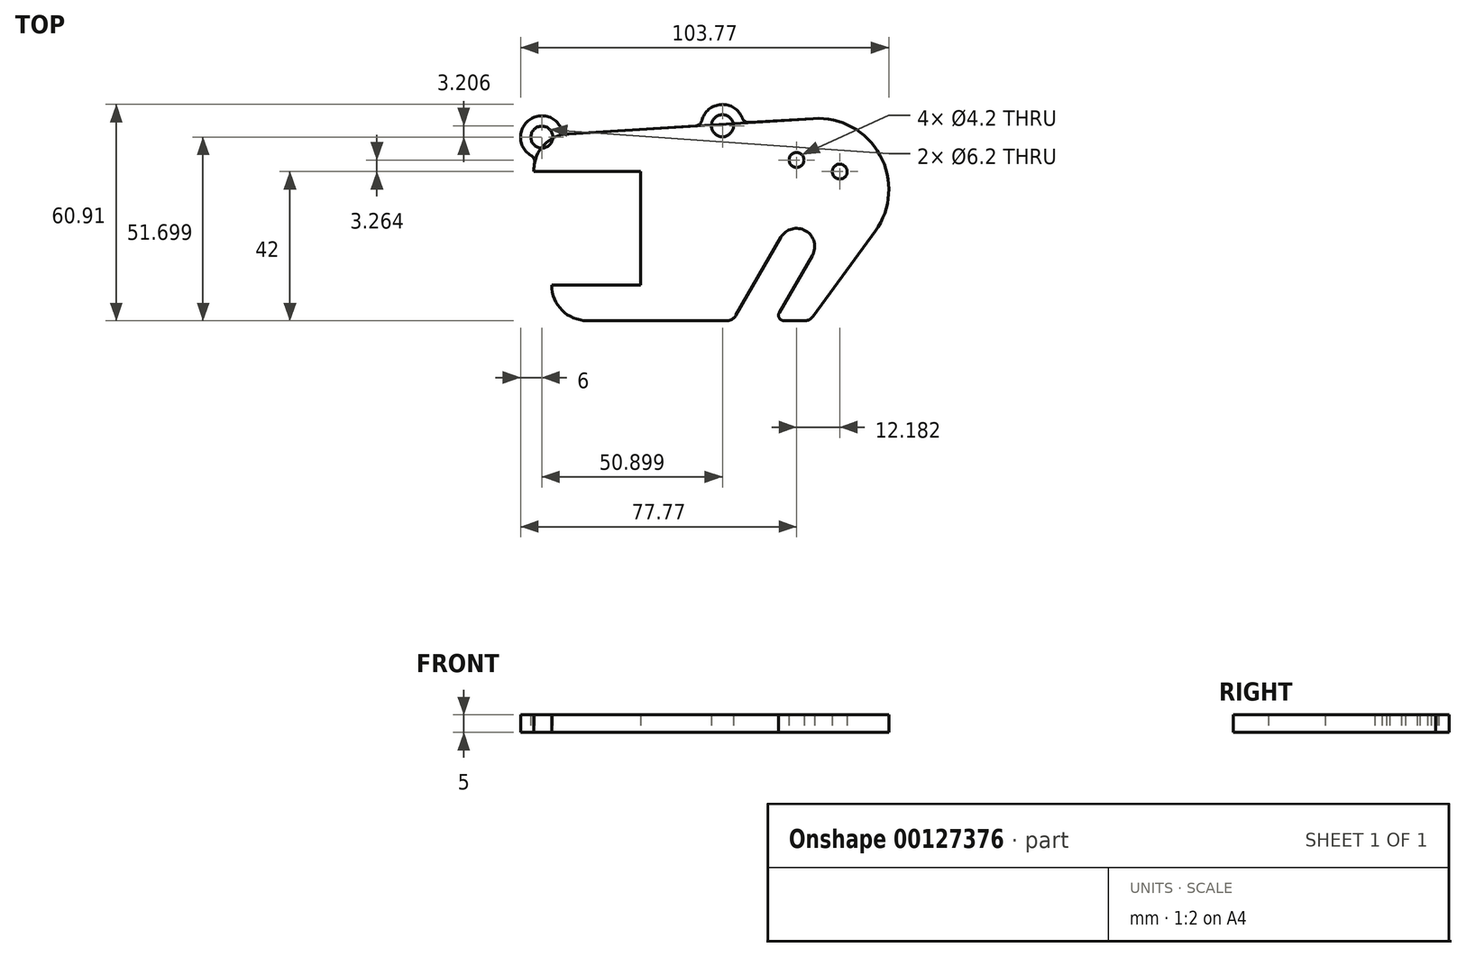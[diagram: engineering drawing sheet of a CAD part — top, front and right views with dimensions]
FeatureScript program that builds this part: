
annotation { "Feature Type Name" : "Feature", "Feature Type Description" : "" }
export const myFeature = defineFeature(function(context is Context, id is Id, definition is map)
    precondition{}
    {
        {
            var Q0;
            Q0=qCreatedBy(makeId("Top.planeOp"),FACE);
            var sketch = newSketch(context, id + "F0", { "sketchPlane" : qUnion([Q0])});
            skLineSegment(sketch, "E0", {"start": v(-25, 17) * mm, "end": v(-25, -15) * mm});
            skLineSegment(sketch, "E1", {"start": v(-25, 1) * mm, "end": v(19, 1) * mm, "construction": true});
            skLineSegment(sketch, "E2", {"start": v(19, 1) * mm, "end": v(19, -4.1) * mm, "construction": true});
            skLineSegment(sketch, "E3", {"start": v(-25, 17) * mm, "end": v(25, 17) * mm, "construction": true});
            skArc(sketch, "E4", {"start": v(23.42, -6.65) * mm, "mid": v(21.55, 0.32) * mm, "end": v(14.58, -1.55) * mm});
            skLineSegment(sketch, "E5", {"start": v(-25, 17) * mm, "end": v(-55, 17) * mm});
            skLineSegment(sketch, "E6", {"start": v(-25, -15) * mm, "end": v(-50, -15) * mm});
            skLineSegment(sketch, "E7", {"start": v(-50, -15) * mm, "end": v(-50, -15) * mm});
            skLineSegment(sketch, "E8", {"start": v(-40, -25) * mm, "end": v(-0.69, -25) * mm});
            skLineSegment(sketch, "E9", {"start": v(-55, 17) * mm, "end": v(-55, 17.61) * mm});
            skLineSegment(sketch, "E10", {"start": v(14.58, -1.55) * mm, "end": v(1.91, -23.5) * mm});
            skLineSegment(sketch, "E11", {"start": v(-45.63, 27.6) * mm, "end": v(23.74, 31.96) * mm});
            skPoint(sketch, "E12.visualSharp", {"position": v(67.74, 34.73) * mm});
            skArc(sketch, "E12.filletArc", {"start": v(41.18, 0.24) * mm, "mid": v(42.53, 21.63) * mm, "end": v(23.74, 31.96) * mm});
            skLineSegment(sketch, "E13", {"start": v(25, 12) * mm, "end": v(25, 17) * mm, "construction": true});
            skLineSegment(sketch, "E14", {"start": v(15.42, -25) * mm, "end": v(21.3, -25) * mm});
            skLineSegment(sketch, "E15", {"start": v(23.42, -6.65) * mm, "end": v(14.12, -22.75) * mm});
            skLineSegment(sketch, "E16", {"start": v(41.18, 0.24) * mm, "end": v(23.72, -23.76) * mm});
            skLineSegment(sketch, "E17", {"start": v(25, 17) * mm, "end": v(31.18, 17) * mm, "construction": true});
            skLineSegment(sketch, "E18", {"start": v(19, -4.1) * mm, "end": v(31.18, 17) * mm, "construction": true});
            skLineSegment(sketch, "E19", {"start": v(19, 1) * mm, "end": v(19, 20.26) * mm, "construction": true});
            skArc(sketch, "E20", {"start": v(31.18, 17) * mm, "mid": v(25.3, 19.43) * mm, "end": v(19, 20.26) * mm, "construction": true});
            skCircle(sketch, "E21", {"center": v(31.18, 17) * mm, "radius": 2.1 * mm});
            skCircle(sketch, "E22", {"center": v(19, 20.26) * mm, "radius": 2.1 * mm});
            skPoint(sketch, "E23.visualSharp", {"position": v(-55, 27) * mm});
            skArc(sketch, "E23.filletArc", {"start": v(-45.63, 27.6) * mm, "mid": v(-52.29, 24.46) * mm, "end": v(-55, 17.61) * mm});
            skPoint(sketch, "E24.visualSharp", {"position": v(-50, -25) * mm});
            skArc(sketch, "E24.filletArc", {"start": v(-50, -15) * mm, "mid": v(-47.07, -22.07) * mm, "end": v(-40, -25) * mm});
            skPoint(sketch, "E25.visualSharp", {"position": v(1.04, -25) * mm});
            skArc(sketch, "E25.filletArc", {"start": v(-0.69, -25) * mm, "mid": v(0.81, -24.6) * mm, "end": v(1.91, -23.5) * mm});
            skPoint(sketch, "E26.visualSharp", {"position": v(12.82, -25) * mm});
            skArc(sketch, "E26.filletArc", {"start": v(14.12, -22.75) * mm, "mid": v(14.12, -24.25) * mm, "end": v(15.42, -25) * mm});
            skPoint(sketch, "E27.visualSharp", {"position": v(22.82, -25) * mm});
            skArc(sketch, "E27.filletArc", {"start": v(21.3, -25) * mm, "mid": v(22.66, -24.67) * mm, "end": v(23.72, -23.76) * mm});
            skLineSegment(sketch, "E28", {"start": v(-25, -15) * mm, "end": v(0, -15) * mm, "construction": true});
            skLineSegment(sketch, "E29", {"start": v(0, -15) * mm, "end": v(0, 0) * mm, "construction": true});
            skSolve(sketch);
        }
        {
            var Q0;
            Q0=makeQuery(id+"F0.imprint","IMPRINT",FACE,{"disambiguationData":[TD([[makeQuery(id+"F0.imprint","IMPRINT",EDGE,{"derivedFrom":sQuery(id+"F0.wireOp",EDGE,"E0")}),1.0]])]});
            extrude(context, id + "F1", {"entities" : qUnion([Q0]), "depth" : 5 * mm});
        }
        {
            var Q0;
            Q0=qCreatedBy(makeId("Top.planeOp"),FACE);
            var sketch = newSketch(context, id + "F2", { "sketchPlane" : qUnion([Q0])});
            skLineSegment(sketch, "E30", {"start": v(-25, 17) * mm, "end": v(-25, -15) * mm});
            skLineSegment(sketch, "E31", {"start": v(-25, 1) * mm, "end": v(19, 1) * mm, "construction": true});
            skLineSegment(sketch, "E32", {"start": v(19, 1) * mm, "end": v(19, -4.1) * mm, "construction": true});
            skLineSegment(sketch, "E33", {"start": v(-25, 17) * mm, "end": v(25, 17) * mm, "construction": true});
            skArc(sketch, "E34", {"start": v(23.42, -6.65) * mm, "mid": v(21.55, 0.32) * mm, "end": v(14.58, -1.55) * mm});
            skLineSegment(sketch, "E35", {"start": v(-25, 17) * mm, "end": v(-55, 17) * mm});
            skLineSegment(sketch, "E36", {"start": v(-25, -15) * mm, "end": v(-50, -15) * mm});
            skLineSegment(sketch, "E37", {"start": v(-50, -15) * mm, "end": v(-50, -15) * mm});
            skLineSegment(sketch, "E38", {"start": v(-40, -25) * mm, "end": v(-0.69, -25) * mm});
            skLineSegment(sketch, "E39", {"start": v(-55, 17) * mm, "end": v(-55, 17.61) * mm});
            skLineSegment(sketch, "E40", {"start": v(14.58, -1.55) * mm, "end": v(1.91, -23.5) * mm});
            skLineSegment(sketch, "E41", {"start": v(-45.2, 27.62) * mm, "end": v(-9.5, 29.87) * mm});
            skPoint(sketch, "E42.visualSharp", {"position": v(67.74, 34.73) * mm});
            skArc(sketch, "E42.filletArc", {"start": v(41.18, 0.24) * mm, "mid": v(42.53, 21.63) * mm, "end": v(23.74, 31.96) * mm});
            skLineSegment(sketch, "E43", {"start": v(25, 12) * mm, "end": v(25, 17) * mm, "construction": true});
            skLineSegment(sketch, "E44", {"start": v(15.42, -25) * mm, "end": v(21.3, -25) * mm});
            skLineSegment(sketch, "E45", {"start": v(23.42, -6.65) * mm, "end": v(14.12, -22.75) * mm});
            skLineSegment(sketch, "E46", {"start": v(41.18, 0.24) * mm, "end": v(23.72, -23.76) * mm});
            skLineSegment(sketch, "E47", {"start": v(25, 17) * mm, "end": v(31.18, 17) * mm, "construction": true});
            skLineSegment(sketch, "E48", {"start": v(19, -4.1) * mm, "end": v(31.18, 17) * mm, "construction": true});
            skLineSegment(sketch, "E49", {"start": v(19, 1) * mm, "end": v(19, 20.26) * mm, "construction": true});
            skArc(sketch, "E50", {"start": v(31.18, 17) * mm, "mid": v(25.3, 19.43) * mm, "end": v(19, 20.26) * mm, "construction": true});
            skCircle(sketch, "E51", {"center": v(31.18, 17) * mm, "radius": 2.1 * mm});
            skCircle(sketch, "E52", {"center": v(19, 20.26) * mm, "radius": 2.1 * mm});
            skPoint(sketch, "E53.visualSharp", {"position": v(-55, 27) * mm});
            skArc(sketch, "E53.filletArc", {"start": v(-54.83, 19.43) * mm, "mid": v(-54.96, 18.52) * mm, "end": v(-55, 17.61) * mm});
            skPoint(sketch, "E54.visualSharp", {"position": v(-50, -25) * mm});
            skArc(sketch, "E54.filletArc", {"start": v(-50, -15) * mm, "mid": v(-47.07, -22.07) * mm, "end": v(-40, -25) * mm});
            skPoint(sketch, "E55.visualSharp", {"position": v(1.04, -25) * mm});
            skArc(sketch, "E55.filletArc", {"start": v(-0.69, -25) * mm, "mid": v(0.81, -24.6) * mm, "end": v(1.91, -23.5) * mm});
            skPoint(sketch, "E56.visualSharp", {"position": v(12.82, -25) * mm});
            skArc(sketch, "E56.filletArc", {"start": v(14.12, -22.75) * mm, "mid": v(14.12, -24.25) * mm, "end": v(15.42, -25) * mm});
            skPoint(sketch, "E57.visualSharp", {"position": v(22.82, -25) * mm});
            skArc(sketch, "E57.filletArc", {"start": v(21.3, -25) * mm, "mid": v(22.66, -24.67) * mm, "end": v(23.72, -23.76) * mm});
            skLineSegment(sketch, "E58", {"start": v(-25, -15) * mm, "end": v(0, -15) * mm, "construction": true});
            skLineSegment(sketch, "E59", {"start": v(0, -15) * mm, "end": v(0, 0) * mm, "construction": true});
            skLineSegment(sketch, "E60", {"start": v(19, -4.1) * mm, "end": v(-1.87, 29.9) * mm, "construction": true});
            skLineSegment(sketch, "E61", {"start": v(-1.87, 29.9) * mm, "end": v(-52.77, 26.7) * mm, "construction": true});
            skLineSegment(sketch, "E62", {"start": v(-52.77, 26.7) * mm, "end": v(19, -4.1) * mm, "construction": true});
            skArc(sketch, "E63", {"start": v(3.72, 32.1) * mm, "mid": v(-2.25, 35.9) * mm, "end": v(-7.69, 31.37) * mm});
            skArc(sketch, "E64", {"start": v(-47.18, 28.89) * mm, "mid": v(-56.67, 31.26) * mm, "end": v(-55.8, 21.52) * mm});
            skCircle(sketch, "E65", {"center": v(-1.87, 29.9) * mm, "radius": 3.1 * mm});
            skCircle(sketch, "E66", {"center": v(-52.77, 26.7) * mm, "radius": 3.1 * mm});
            skArc(sketch, "E67.filletArc", {"start": v(-47.18, 28.89) * mm, "mid": v(-46.4, 27.93) * mm, "end": v(-45.2, 27.62) * mm});
            skArc(sketch, "E68.filletArc", {"start": v(-54.83, 19.43) * mm, "mid": v(-54.98, 20.62) * mm, "end": v(-55.8, 21.52) * mm});
            skLineSegment(sketch, "E69.trimOffspring", {"start": v(5.7, 30.82) * mm, "end": v(23.74, 31.96) * mm});
            skPoint(sketch, "E70.visualSharp", {"position": v(-7.87, 29.97) * mm});
            skArc(sketch, "E70.filletArc", {"start": v(-9.5, 29.87) * mm, "mid": v(-8.35, 30.32) * mm, "end": v(-7.69, 31.37) * mm});
            skPoint(sketch, "E71.visualSharp", {"position": v(4.07, 30.72) * mm});
            skArc(sketch, "E71.filletArc", {"start": v(3.72, 32.1) * mm, "mid": v(4.5, 31.13) * mm, "end": v(5.7, 30.82) * mm});
            skSolve(sketch);
        }
        {
            var Q0;
            Q0 = qSketchRegion(id + "F2", true);
            extrude(context, id + "F3", {"entities" : qUnion([Q0]), "depth" : 5 * mm});
        }
    });
